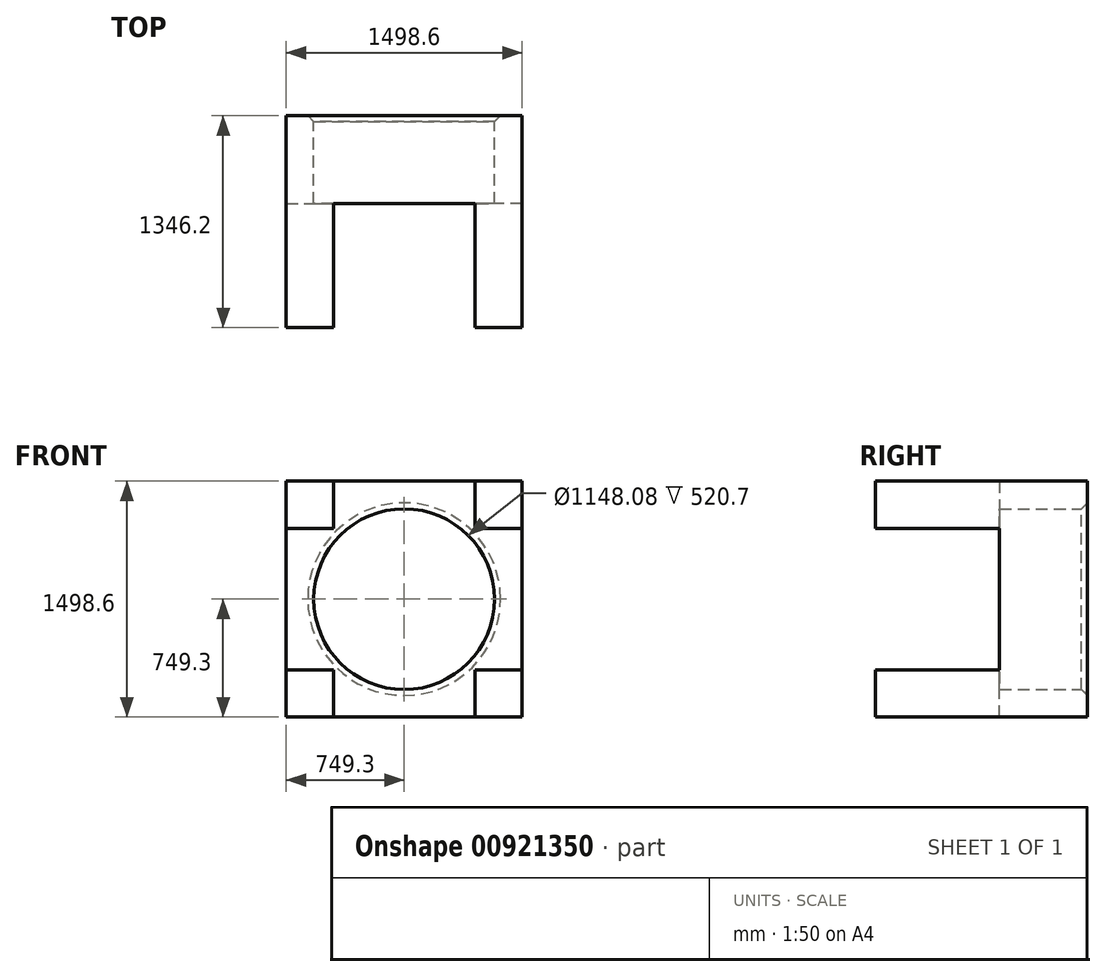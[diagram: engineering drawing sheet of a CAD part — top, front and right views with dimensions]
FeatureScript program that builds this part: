
annotation { "Feature Type Name" : "Feature", "Feature Type Description" : "" }
export const myFeature = defineFeature(function(context is Context, id is Id, definition is map)
    precondition{}
    {
        {
            var Q0;
            Q0=qCreatedBy(makeId("Front.planeOp"),FACE);
            var sketch = newSketch(context, id + "F0", { "sketchPlane" : qUnion([Q0])});
            skCircle(sketch, "E0", {"center": v(0, 0) * mm, "radius": 574.04 * mm});
            skLineSegment(sketch, "E1.bottom", {"start": v(-749.3, -749.3) * mm, "end": v(749.3, -749.3) * mm});
            skLineSegment(sketch, "E1.top", {"start": v(-749.3, 749.3) * mm, "end": v(749.3, 749.3) * mm});
            skLineSegment(sketch, "E1.left", {"start": v(-749.3, -749.3) * mm, "end": v(-749.3, 749.3) * mm});
            skLineSegment(sketch, "E1.right", {"start": v(749.3, -749.3) * mm, "end": v(749.3, 749.3) * mm});
            skSolve(sketch);
        }
        {
            var Q0;
            Q0=makeQuery(id+"F0.imprint","IMPRINT",FACE,{"disambiguationData":[TD([[makeQuery(id+"F0.imprint","IMPRINT",EDGE,{"derivedFrom":sQuery(id+"F0.wireOp",EDGE,"E0")}),-1.0]])]});
            extrude(context, id + "F1", {"entities" : qUnion([Q0]), "depth" : 558.8 * mm, "offsetDistance" : 25.4 * mm});
        }
        {
            var Q0;
            Q0=makeQuery(id+"F1.opExtrude","CAP_FACE",FACE,{"disambiguationData":[OSD([sQuery(id+"F0.wireOp",EDGE,"E0"),sQuery(id+"F0.wireOp",EDGE,"E1.bottom"),sQuery(id+"F0.wireOp",EDGE,"E1.top"),sQuery(id+"F0.wireOp",EDGE,"E1.left"),sQuery(id+"F0.wireOp",EDGE,"E1.right")])],"isStart":false});
            var sketch = newSketch(context, id + "F2", { "sketchPlane" : qUnion([Q0])});
            skLineSegment(sketch, "E2.bottom", {"start": v(-749.3, 749.3) * mm, "end": v(-449.58, 749.3) * mm});
            skLineSegment(sketch, "E2.top", {"start": v(-749.3, 449.58) * mm, "end": v(-449.58, 449.58) * mm});
            skLineSegment(sketch, "E2.left", {"start": v(-749.3, 749.3) * mm, "end": v(-749.3, 449.58) * mm});
            skLineSegment(sketch, "E2.right", {"start": v(-449.58, 749.3) * mm, "end": v(-449.58, 449.58) * mm});
            skLineSegment(sketch, "E3.bottom", {"start": v(-749.3, -749.3) * mm, "end": v(-449.58, -749.3) * mm});
            skLineSegment(sketch, "E3.top", {"start": v(-749.3, -449.58) * mm, "end": v(-449.58, -449.58) * mm});
            skLineSegment(sketch, "E3.left", {"start": v(-749.3, -749.3) * mm, "end": v(-749.3, -449.58) * mm});
            skLineSegment(sketch, "E3.right", {"start": v(-449.58, -749.3) * mm, "end": v(-449.58, -449.58) * mm});
            skLineSegment(sketch, "E4.bottom", {"start": v(749.3, -749.3) * mm, "end": v(449.58, -749.3) * mm});
            skLineSegment(sketch, "E4.top", {"start": v(749.3, -449.58) * mm, "end": v(449.58, -449.58) * mm});
            skLineSegment(sketch, "E4.left", {"start": v(749.3, -749.3) * mm, "end": v(749.3, -449.58) * mm});
            skLineSegment(sketch, "E4.right", {"start": v(449.58, -749.3) * mm, "end": v(449.58, -449.58) * mm});
            skLineSegment(sketch, "E5.bottom", {"start": v(749.3, 749.3) * mm, "end": v(449.58, 749.3) * mm});
            skLineSegment(sketch, "E5.top", {"start": v(749.3, 449.58) * mm, "end": v(449.58, 449.58) * mm});
            skLineSegment(sketch, "E5.left", {"start": v(749.3, 749.3) * mm, "end": v(749.3, 449.58) * mm});
            skLineSegment(sketch, "E5.right", {"start": v(449.58, 749.3) * mm, "end": v(449.58, 449.58) * mm});
            skSolve(sketch);
        }
        {
            var Q0;
            Q0 = qSketchRegion(id + "F2", true);
            extrude(context, id + "F3", {"entities" : qUnion([Q0]), "operationType" : NewBodyOperationType.ADD, "depth" : 787.4 * mm, "offsetDistance" : 25.4 * mm});
        }
        {
            var Q0;
            Q0=makeQuery(id+"F1.opExtrude","CAP_EDGE",EDGE,{"disambiguationData":[OSD([sQuery(id+"F0.wireOp",EDGE,"E0")])],"isStart":true});
            chamfer(context, id + "F4", {"entities" : qUnion([Q0]), "width" : 38.1 * mm, "tangentPropagation" : true});
        }
    });
